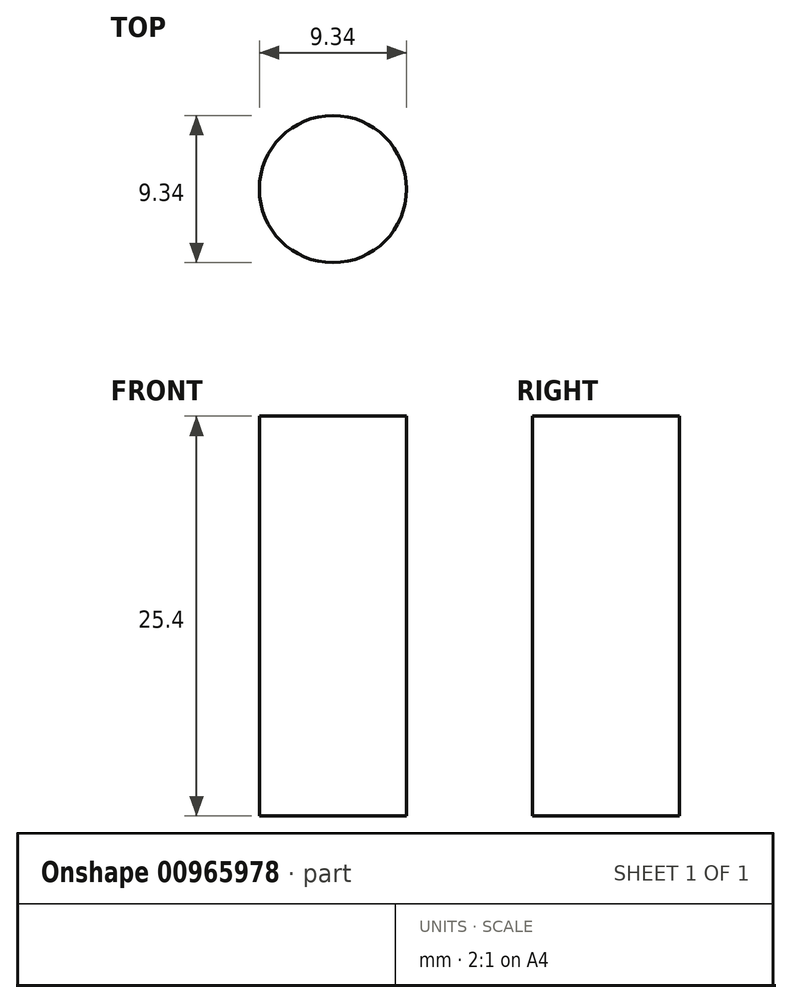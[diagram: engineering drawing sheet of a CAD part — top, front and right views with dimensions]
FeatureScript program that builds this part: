
annotation { "Feature Type Name" : "Feature", "Feature Type Description" : "" }
export const myFeature = defineFeature(function(context is Context, id is Id, definition is map)
    precondition{}
    {
        {
            var Q0;
            Q0=qCreatedBy(makeId("Top.planeOp"),FACE);
            var sketch = newSketch(context, id + "F0", { "sketchPlane" : qUnion([Q0])});
            skCircle(sketch, "E0", {"center": v(0, 0) * mm, "radius": 4.67 * mm});
            skSolve(sketch);
        }
        {
            var Q0;
            Q0=makeQuery(id+"F0.imprint","IMPRINT",FACE,{"disambiguationData":[TD([[makeQuery(id+"F0.imprint","IMPRINT",EDGE,{"derivedFrom":sQuery(id+"F0.wireOp",EDGE,"E0")}),1.0]])]});
            extrude(context, id + "F1", {"entities" : qUnion([Q0]), "depth" : 25.4 * mm, "offsetDistance" : 25.4 * mm});
        }
    });
